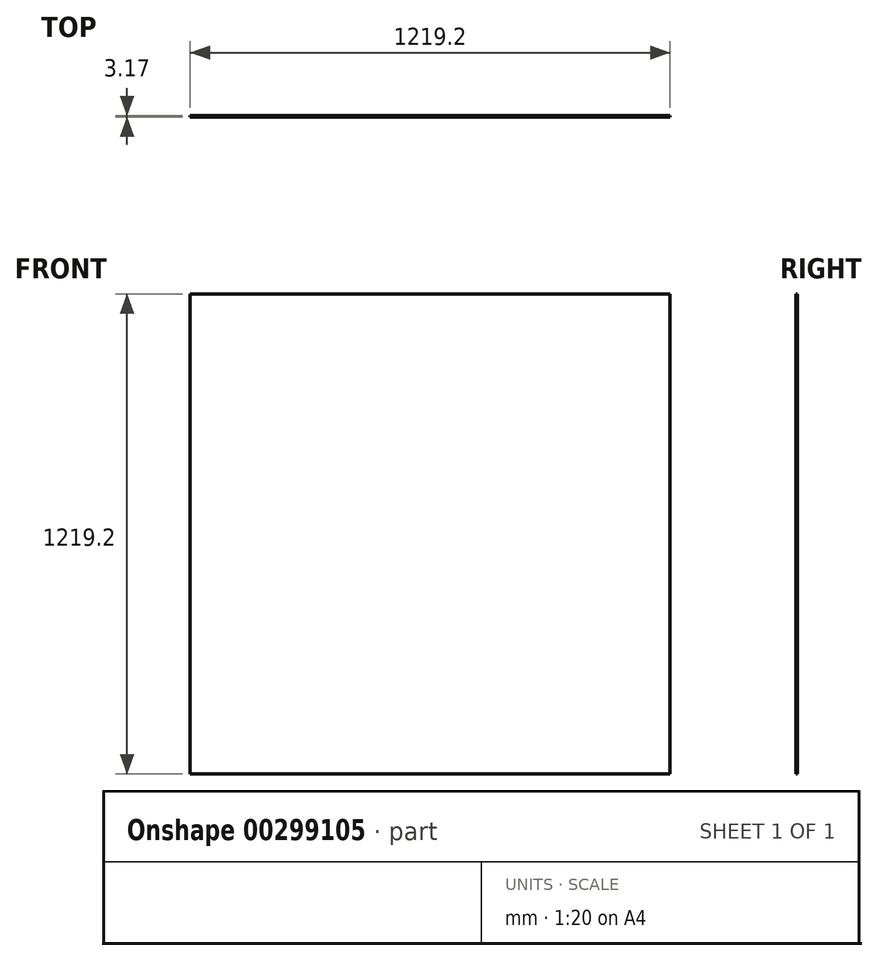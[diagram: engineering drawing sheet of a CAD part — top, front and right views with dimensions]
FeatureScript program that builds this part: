
annotation { "Feature Type Name" : "Feature", "Feature Type Description" : "" }
export const myFeature = defineFeature(function(context is Context, id is Id, definition is map)
    precondition{}
    {
        {
            var Q0;
            Q0=qCreatedBy(makeId("Front.planeOp"),FACE);
            var sketch = newSketch(context, id + "F0", { "sketchPlane" : qUnion([Q0])});
            skLineSegment(sketch, "E0.bottom", {"start": v(-606.74, 609.6) * mm, "end": v(612.46, 609.6) * mm});
            skLineSegment(sketch, "E0.top", {"start": v(-606.74, -609.6) * mm, "end": v(612.46, -609.6) * mm});
            skLineSegment(sketch, "E0.left", {"start": v(-606.74, 609.6) * mm, "end": v(-606.74, -609.6) * mm});
            skLineSegment(sketch, "E0.right", {"start": v(612.46, 609.6) * mm, "end": v(612.46, -609.6) * mm});
            skPoint(sketch, "E0.middle", {"position": v(2.86, 0) * mm});
            skSolve(sketch);
        }
        {
            var Q0;
            Q0 = qSketchRegion(id + "F0", true);
            extrude(context, id + "F1", {"entities" : qUnion([Q0]), "depth" : 3.17 * mm});
        }
    });
